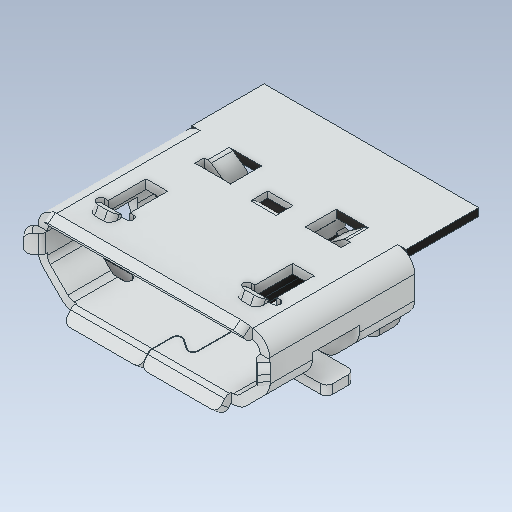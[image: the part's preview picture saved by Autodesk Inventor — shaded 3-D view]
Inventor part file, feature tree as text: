
AUTODESK INVENTOR PART (.ipt)
format: ipt  version: 2020.1 (Build 241239000, 239)  size: 541,184 bytes
history: mixed  units: mm
features: extrude x2, sketch x2, fillet x1, imported_body x1
ambient origin geometry x8: Origin, YZ Plane, XZ Plane, XY Plane, X Axis, Y Axis, Z Axis, Center Point
bodies: Solid1 (imported_parasolid)
feature tree (6):
  extrude  "Extrusion1"  Depth=4.7mm
  extrude  "Extrusion2"  Depth=0.5mm
  sketch  "Sketch1"  dims[d0=2.35mm d1=4.7mm]
  sketch  "Sketch2"  dims[d2=0.25mm d3=0.0mm d4=0.5mm d5=50.0mm d7=1.3mm d8=10.0mm d10=10.0mm d13=0.1mm d14=0.0mm]
  fillet  "Fillet13"  Radius=1.3mm
  imported_body  NMx_Import_Brep_tag  [imported B-rep: ~345 faces, bbox_mm=[7.98, 2.783674, 7.48]]
